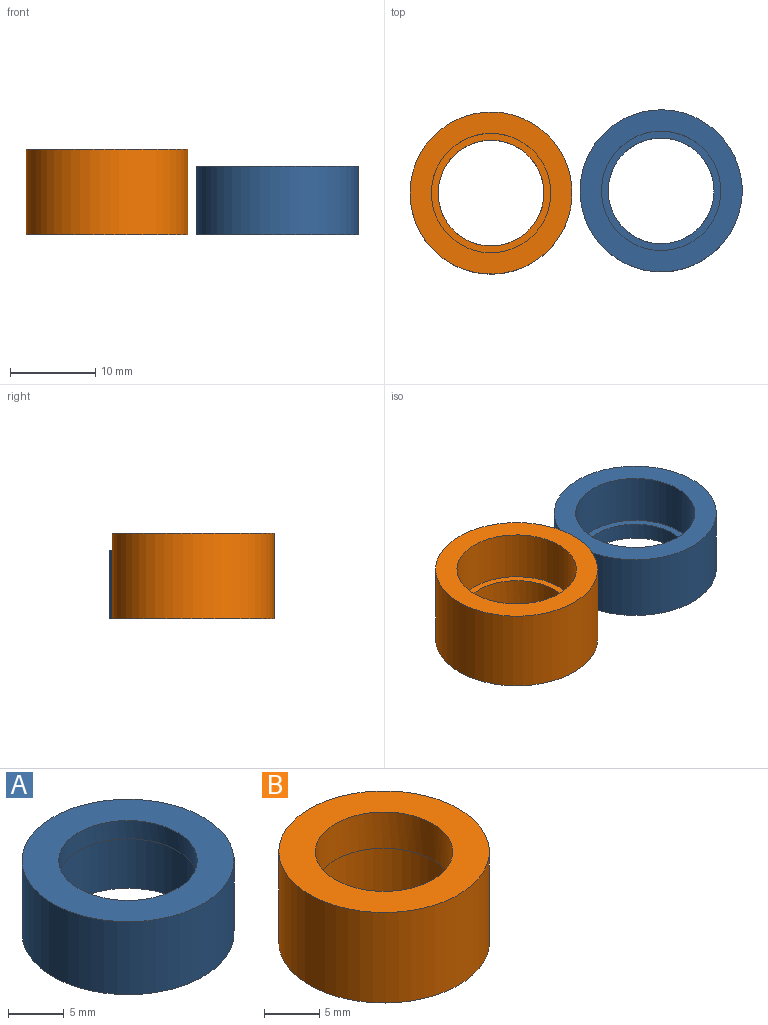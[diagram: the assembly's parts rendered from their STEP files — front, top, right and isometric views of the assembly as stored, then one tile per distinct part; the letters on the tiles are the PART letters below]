
ASSEMBLY  parts=2 mates=1
PART A: 6 faces, bbox 19x19x8 mm
  f0: cylinder r=9.5mm len=19mm, axis (0,0,-1), area 477.5mm2, adj f2,f5
  f1: cylinder r=6.2mm len=12.4mm, axis (0,0,-1), area 77.9mm2, adj f4,f5
  f2: plane 19x19mm, normal (0,0,-1), area 129.6mm2, adj f0,f3
  f3: cylinder r=7mm len=14mm, axis (0,0,-1), area 263.9mm2, adj f2,f4
  f4: plane 14x14mm, normal (0,0,-1), area 33.2mm2, adj f1,f3
  f5: plane 19x19mm, normal (0,0,1), area 162.8mm2, adj f0,f1
PART B: 6 faces, bbox 19x19x10 mm
  f0: cylinder r=9.5mm len=19mm, axis (0,0,-1), area 596.9mm2, adj f1,f2
  f1: plane 19x19mm, normal (0,0,1), area 162.8mm2, adj f0,f5
  f2: plane 19x19mm, normal (0,0,-1), area 129.6mm2, adj f0,f3
  f3: cylinder r=7mm len=14mm, axis (0,0,-1), area 263.9mm2, adj f2,f4
  f4: plane 14x14mm, normal (0,0,-1), area 33.2mm2, adj f3,f5
  f5: cylinder r=6.2mm len=12.4mm, axis (0,0,-1), area 155.8mm2, adj f1,f4
PLACE A rot(axis=(0,1,0),180deg) t=(-15.3,-26.41,-11.3)mm
PLACE B rot(axis=(0,1,0),180deg) t=(-35.23,-26.68,-9.3)mm
MATE planar A.f0 <-> B.f0  axis (0,0,-1) through (-15.3,-26.41,-19.3)mm
